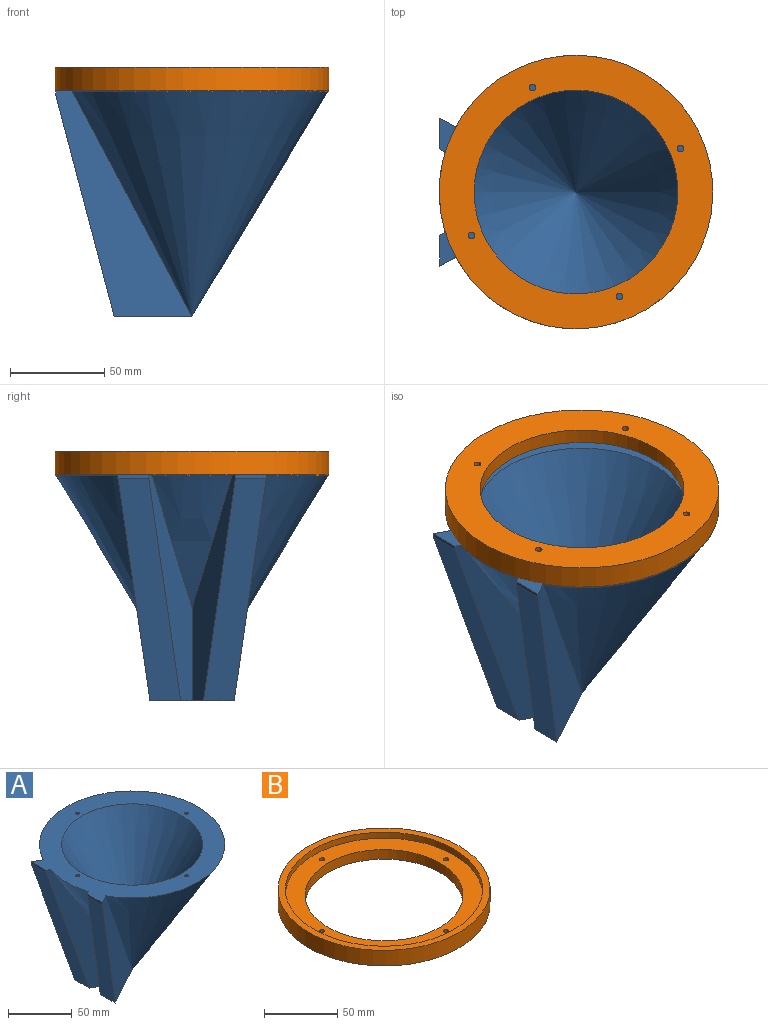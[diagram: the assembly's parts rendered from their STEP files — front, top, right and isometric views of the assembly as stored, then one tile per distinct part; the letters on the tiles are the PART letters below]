
ASSEMBLY  parts=2 mates=1
PART A: 21 faces, bbox 144.9x144.9x120 mm
  f0: plane 44.71x41.14mm, normal (0,0,-1), area 852.7mm2, adj f2,f3,f8,f9,f10,f11
  f1: plane 16.32x1.96mm, normal (-1,0,0), area 32mm2, adj f2,f3,f6,f11
  f2: plane 120x42.24mm, normal (-0.48,-0.88,0), area 2086.1mm2, adj f0,f1,f5,f6,f8,f11
  f3: plane 120x72.27mm, normal (0.48,0.88,0), area 3432.3mm2, adj f0,f1,f4,f6,f11
  f4: cone r=72.45mm half-angle=31.1deg, axis (0,0,1), area 26849.9mm2, adj f3,f6,f9
  f5: cone r=72.45mm half-angle=31.1deg, axis (0,0,1), area 1793.7mm2, adj f2,f6,f8
  f6: plane 144.9x144.9mm, normal (0,0,1), area 7112.4mm2, adj f1,f2,f3,f4,f5,f7,f8,f9
  f7: plane 16.32x1.96mm, normal (-1,0,0), area 32mm2, adj f6,f8,f9,f10
  f8: plane 120x42.24mm, normal (-0.48,0.88,0), area 2086.1mm2, adj f0,f2,f5,f6,f7,f10
  f9: plane 120x72.27mm, normal (0.48,-0.88,0), area 3432.3mm2, adj f0,f4,f6,f7,f10
  f10: plane 118.04x33.23mm, normal (-0.97,0,-0.25), area 1992mm2, adj f0,f7,f8,f9
  f11: plane 118.04x33.23mm, normal (-0.97,0,-0.25), area 1992mm2, adj f0,f1,f2,f3
  f12: cone r=55.08mm half-angle=31.1deg, axis (0,0,1), area 18443.2mm2, adj f6
  f13: cylinder r=1.5mm len=10mm, axis (0,0,1), area 94.2mm2, adj f6,f14
  f14: plane 3x3mm, normal (0,0,1), area 7.1mm2, adj f13
  f15: cylinder r=1.5mm len=10mm, axis (0,0,1), area 94.2mm2, adj f6,f16
  f16: plane 3x3mm, normal (0,0,1), area 7.1mm2, adj f15
  f17: cylinder r=1.5mm len=10mm, axis (0,0,1), area 94.2mm2, adj f6,f18
  f18: plane 3x3mm, normal (0,0,1), area 7.1mm2, adj f17
  f19: cylinder r=1.5mm len=10mm, axis (0,0,1), area 94.2mm2, adj f6,f20
  f20: plane 3x3mm, normal (0,0,1), area 7.1mm2, adj f19
PART B: 10 faces, bbox 145x145x13 mm
  f0: cylinder r=54mm len=108mm, axis (0,0,-1), area 2714.3mm2, adj f6,f7
  f1: cylinder r=1.75mm len=8mm, axis (0,0,-1), area 88mm2, adj f6,f7
  f2: cylinder r=1.75mm len=8mm, axis (0,0,-1), area 88mm2, adj f6,f7
  f3: cylinder r=1.75mm len=8mm, axis (0,0,-1), area 88mm2, adj f6,f7
  f4: cylinder r=1.75mm len=8mm, axis (0,0,-1), area 88mm2, adj f6,f7
  f5: cylinder r=72.5mm len=145mm, axis (0,0,-1), area 5921.9mm2, adj f7,f9
  f6: plane 135x135mm, normal (0,0,1), area 5114.5mm2, adj f0,f1,f2,f3,f4,f8
  f7: plane 145x145mm, normal (0,0,-1), area 7313.6mm2, adj f0,f1,f2,f3,f4,f5
  f8: cylinder r=67.5mm len=135mm, axis (0,0,-1), area 2120.6mm2, adj f6,f9
  f9: plane 145x145mm, normal (0,0,1), area 2199.1mm2, adj f5,f8
PLACE A rot(axis=(0,0,-1),0deg) t=(-23.6,23.51,-2.32)mm
PLACE B rot(axis=(0.2,-0.98,0),180deg) t=(-23.51,23.51,10.18)mm
MATE parallel B.f0 <-> A.f6  axis (0,0,-1) through (-23.51,23.51,-2.82)mm
